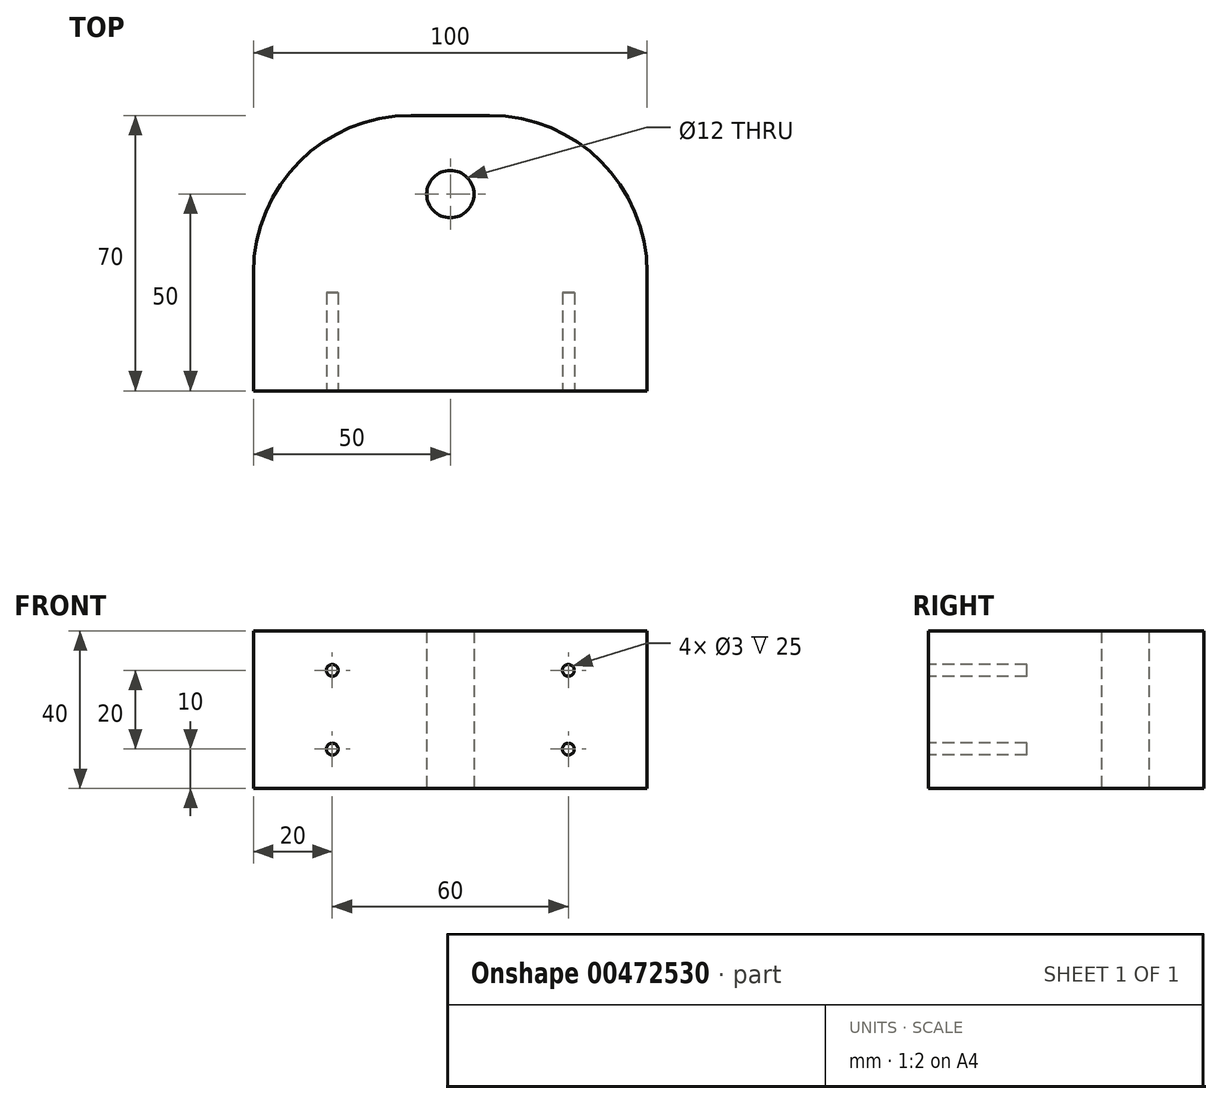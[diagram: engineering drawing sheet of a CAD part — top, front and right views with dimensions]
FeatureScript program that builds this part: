
annotation { "Feature Type Name" : "Feature", "Feature Type Description" : "" }
export const myFeature = defineFeature(function(context is Context, id is Id, definition is map)
    precondition{}
    {
        {
            var Q0;
            Q0=qCreatedBy(makeId("Top.planeOp"),FACE);
            var sketch = newSketch(context, id + "F0", { "sketchPlane" : qUnion([Q0])});
            skLineSegment(sketch, "E0.bottom", {"start": v(50, 0) * mm, "end": v(-50, 0) * mm});
            skLineSegment(sketch, "E0.top", {"start": v(50, 70) * mm, "end": v(-50, 70) * mm});
            skLineSegment(sketch, "E0.left", {"start": v(50, 0) * mm, "end": v(50, 70) * mm});
            skLineSegment(sketch, "E0.right", {"start": v(-50, 0) * mm, "end": v(-50, 70) * mm});
            skPoint(sketch, "E0.middle", {"position": v(0, 35) * mm});
            skCircle(sketch, "E1", {"center": v(0, 50) * mm, "radius": 6 * mm});
            skSolve(sketch);
        }
        {
            var Q0;
            Q0 = qSketchRegion(id + "F0", true);
            extrude(context, id + "F1", {"entities" : qUnion([Q0]), "depth" : 40 * mm, "symmetric" : true});
        }
        {
            var Q0;
            Q0=makeQuery(id+"F1.opExtrude","SWEPT_EDGE",EDGE,{"disambiguationData":[OSD([sQuery(id+"F0.wireOp",EDGE,"E0.top"),sQuery(id+"F0.wireOp",EDGE,"E0.right")])]});
            var Q1;
            Q1=makeQuery(id+"F1.opExtrude","SWEPT_EDGE",EDGE,{"disambiguationData":[OSD([sQuery(id+"F0.wireOp",EDGE,"E0.top"),sQuery(id+"F0.wireOp",EDGE,"E0.left")])]});
            fillet(context, id + "F2", {"entities" : qUnion([Q0, Q1]), "radius" : 40 * mm, "tangentPropagation" : true, "allowEdgeOverflow" : false});
        }
        {
            var Q0;
            Q0=makeQuery(id+"F1.opExtrude","SWEPT_FACE",FACE,{"disambiguationData":[OSD([sQuery(id+"F0.wireOp",EDGE,"E0.bottom")])]});
            var sketch = newSketch(context, id + "F3", { "sketchPlane" : qUnion([Q0])});
            skCircle(sketch, "E2", {"center": v(-30, 10) * mm, "radius": 1.5 * mm});
            skCircle(sketch, "E3", {"center": v(-30, -10) * mm, "radius": 1.5 * mm});
            skCircle(sketch, "E4", {"center": v(30, -10) * mm, "radius": 1.5 * mm});
            skCircle(sketch, "E5", {"center": v(30, 10) * mm, "radius": 1.5 * mm});
            skSolve(sketch);
        }
        {
            var Q0;
            Q0 = qSketchRegion(id + "F3", true);
            extrude(context, id + "F4", {"entities" : qUnion([Q0]), "operationType" : NewBodyOperationType.REMOVE, "oppositeDirection" : true, "depth" : 25 * mm});
        }
    });
